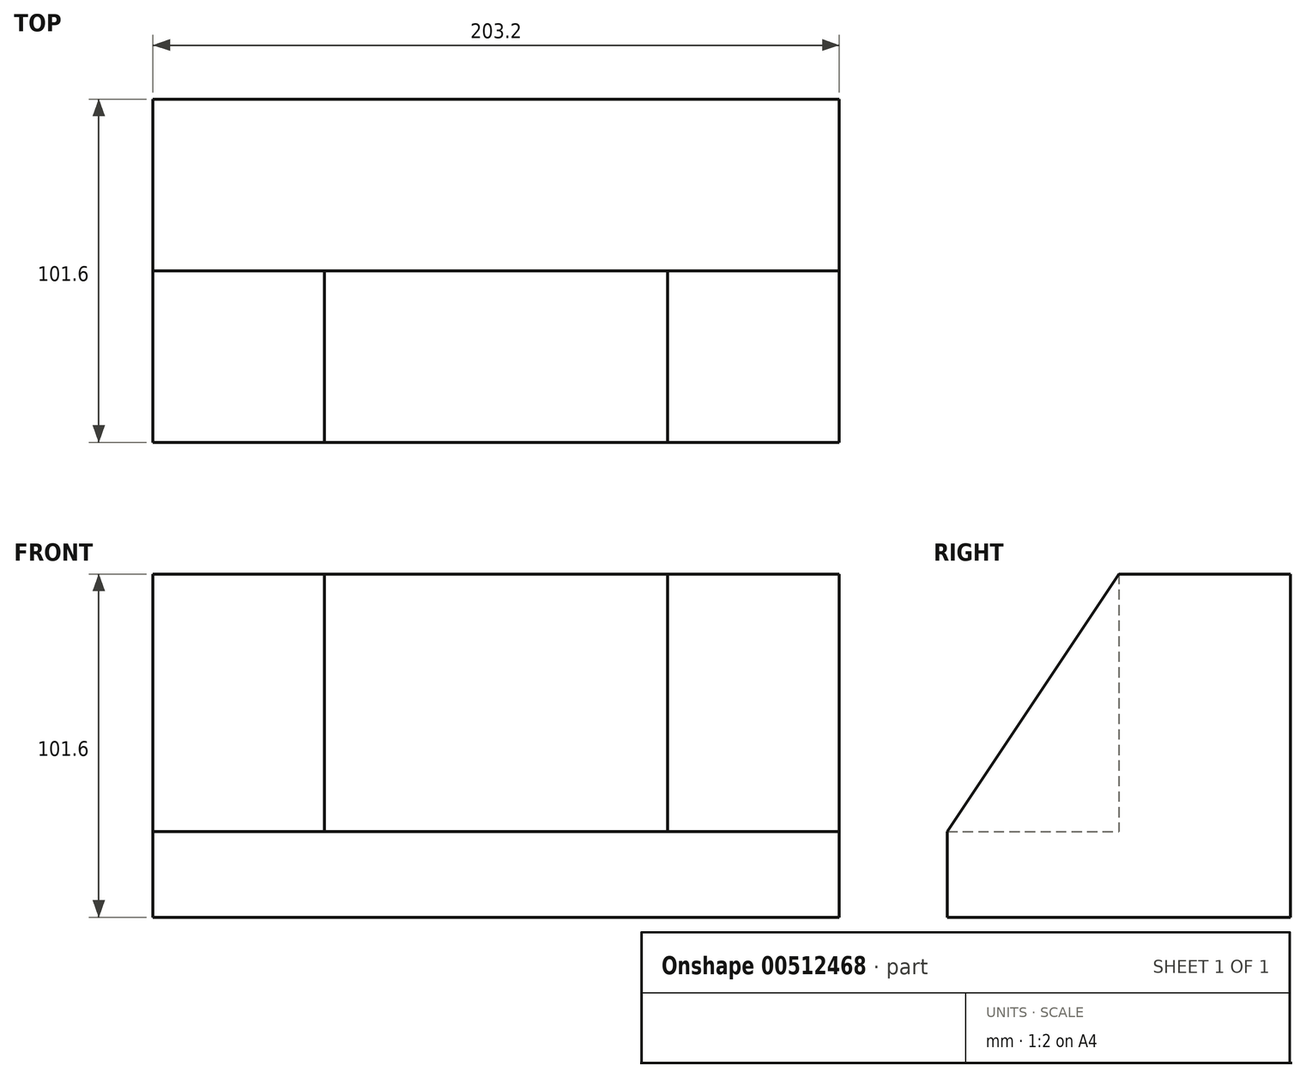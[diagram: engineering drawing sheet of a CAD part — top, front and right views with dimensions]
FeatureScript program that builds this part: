
annotation { "Feature Type Name" : "Feature", "Feature Type Description" : "" }
export const myFeature = defineFeature(function(context is Context, id is Id, definition is map)
    precondition{}
    {
        {
            var Q0;
            Q0=qCreatedBy(makeId("Front.planeOp"),FACE);
            var sketch = newSketch(context, id + "F0", { "sketchPlane" : qUnion([Q0])});
            skLineSegment(sketch, "E0.bottom", {"start": v(0, 0) * mm, "end": v(203.2, 0) * mm});
            skLineSegment(sketch, "E0.top", {"start": v(0, 25.4) * mm, "end": v(203.2, 25.4) * mm});
            skLineSegment(sketch, "E0.left", {"start": v(0, 0) * mm, "end": v(0, 25.4) * mm});
            skLineSegment(sketch, "E0.right", {"start": v(203.2, 0) * mm, "end": v(203.2, 25.4) * mm});
            skSolve(sketch);
        }
        {
            var Q0;
            Q0=makeQuery(id+"F0.imprint","IMPRINT",FACE,{"disambiguationData":[TD([[makeQuery(id+"F0.imprint","IMPRINT",EDGE,{"derivedFrom":sQuery(id+"F0.wireOp",EDGE,"E0.bottom")}),1.0]])]});
            extrude(context, id + "F1", {"entities" : qUnion([Q0]), "depth" : 101.6 * mm});
        }
        {
            var Q0;
            Q0=makeQuery(id+"F1.opExtrude","SWEPT_FACE",FACE,{"disambiguationData":[OSD([sQuery(id+"F0.wireOp",EDGE,"E0.top")])]});
            var sketch = newSketch(context, id + "F2", { "sketchPlane" : qUnion([Q0])});
            skLineSegment(sketch, "E1.bottom", {"start": v(0, 0) * mm, "end": v(203.2, 0) * mm});
            skLineSegment(sketch, "E1.top", {"start": v(0, -50.8) * mm, "end": v(203.2, -50.8) * mm});
            skLineSegment(sketch, "E1.left", {"start": v(0, 0) * mm, "end": v(0, -50.8) * mm});
            skLineSegment(sketch, "E1.right", {"start": v(203.2, 0) * mm, "end": v(203.2, -50.8) * mm});
            skSolve(sketch);
        }
        {
            var Q0;
            Q0=makeQuery(id+"F2.imprint","IMPRINT",FACE,{"disambiguationData":[TD([[makeQuery(id+"F2.imprint","IMPRINT",EDGE,{"derivedFrom":sQuery(id+"F2.wireOp",EDGE,"E1.bottom")}),-1.0]])]});
            extrude(context, id + "F3", {"entities" : qUnion([Q0]), "operationType" : NewBodyOperationType.ADD, "depth" : 76.2 * mm});
        }
        {
            var Q0;
            Q0=makeQuery(id+"F3.opExtrude","SWEPT_FACE",FACE,{"disambiguationData":[OSD([sQuery(id+"F2.wireOp",EDGE,"E1.top")])]});
            var sketch = newSketch(context, id + "F4", { "sketchPlane" : qUnion([Q0])});
            skLineSegment(sketch, "E2.bottom", {"start": v(0, 101.6) * mm, "end": v(50.8, 101.6) * mm});
            skLineSegment(sketch, "E2.top", {"start": v(0, 25.4) * mm, "end": v(50.8, 25.4) * mm});
            skLineSegment(sketch, "E2.left", {"start": v(0, 101.6) * mm, "end": v(0, 25.4) * mm});
            skLineSegment(sketch, "E2.right", {"start": v(50.8, 101.6) * mm, "end": v(50.8, 25.4) * mm});
            skSolve(sketch);
        }
        {
            var Q0;
            Q0 = qSketchRegion(id + "F4", true);
            extrude(context, id + "F5", {"entities" : qUnion([Q0]), "operationType" : NewBodyOperationType.ADD, "depth" : 50.8 * mm});
        }
        {
            var Q0;
            Q0=makeQuery(id+"F5.opExtrude","CAP_EDGE",EDGE,{"disambiguationData":[OSD([sQuery(id+"F4.wireOp",EDGE,"E2.bottom")])],"isStart":false});
            chamfer(context, id + "F6", {"entities" : qUnion([Q0]), "chamferType" : ChamferType.TWO_OFFSETS, "width1" : 50.8 * mm, "oppositeDirection" : false, "width2" : 76.2 * mm});
        }
        {
            var Q0;
            Q0=makeQuery(id+"F3.opExtrude","SWEPT_FACE",FACE,{"disambiguationData":[OSD([sQuery(id+"F2.wireOp",EDGE,"E1.top")])]});
            var sketch = newSketch(context, id + "F7", { "sketchPlane" : qUnion([Q0])});
            skLineSegment(sketch, "E3.bottom", {"start": v(203.2, 101.6) * mm, "end": v(152.4, 101.6) * mm});
            skLineSegment(sketch, "E3.top", {"start": v(203.2, 25.4) * mm, "end": v(152.4, 25.4) * mm});
            skLineSegment(sketch, "E3.left", {"start": v(203.2, 101.6) * mm, "end": v(203.2, 25.4) * mm});
            skLineSegment(sketch, "E3.right", {"start": v(152.4, 101.6) * mm, "end": v(152.4, 25.4) * mm});
            skSolve(sketch);
        }
        {
            var Q0;
            Q0 = qSketchRegion(id + "F7", true);
            extrude(context, id + "F8", {"entities" : qUnion([Q0]), "operationType" : NewBodyOperationType.ADD, "depth" : 50.8 * mm});
        }
        {
            var Q0;
            Q0=makeQuery(id+"F8.opExtrude","CAP_EDGE",EDGE,{"disambiguationData":[OSD([sQuery(id+"F7.wireOp",EDGE,"E3.bottom")])],"isStart":false});
            chamfer(context, id + "F9", {"entities" : qUnion([Q0]), "chamferType" : ChamferType.TWO_OFFSETS, "width1" : 50.8 * mm, "oppositeDirection" : false, "width2" : 76.2 * mm, "tangentPropagation" : true});
        }
    });
